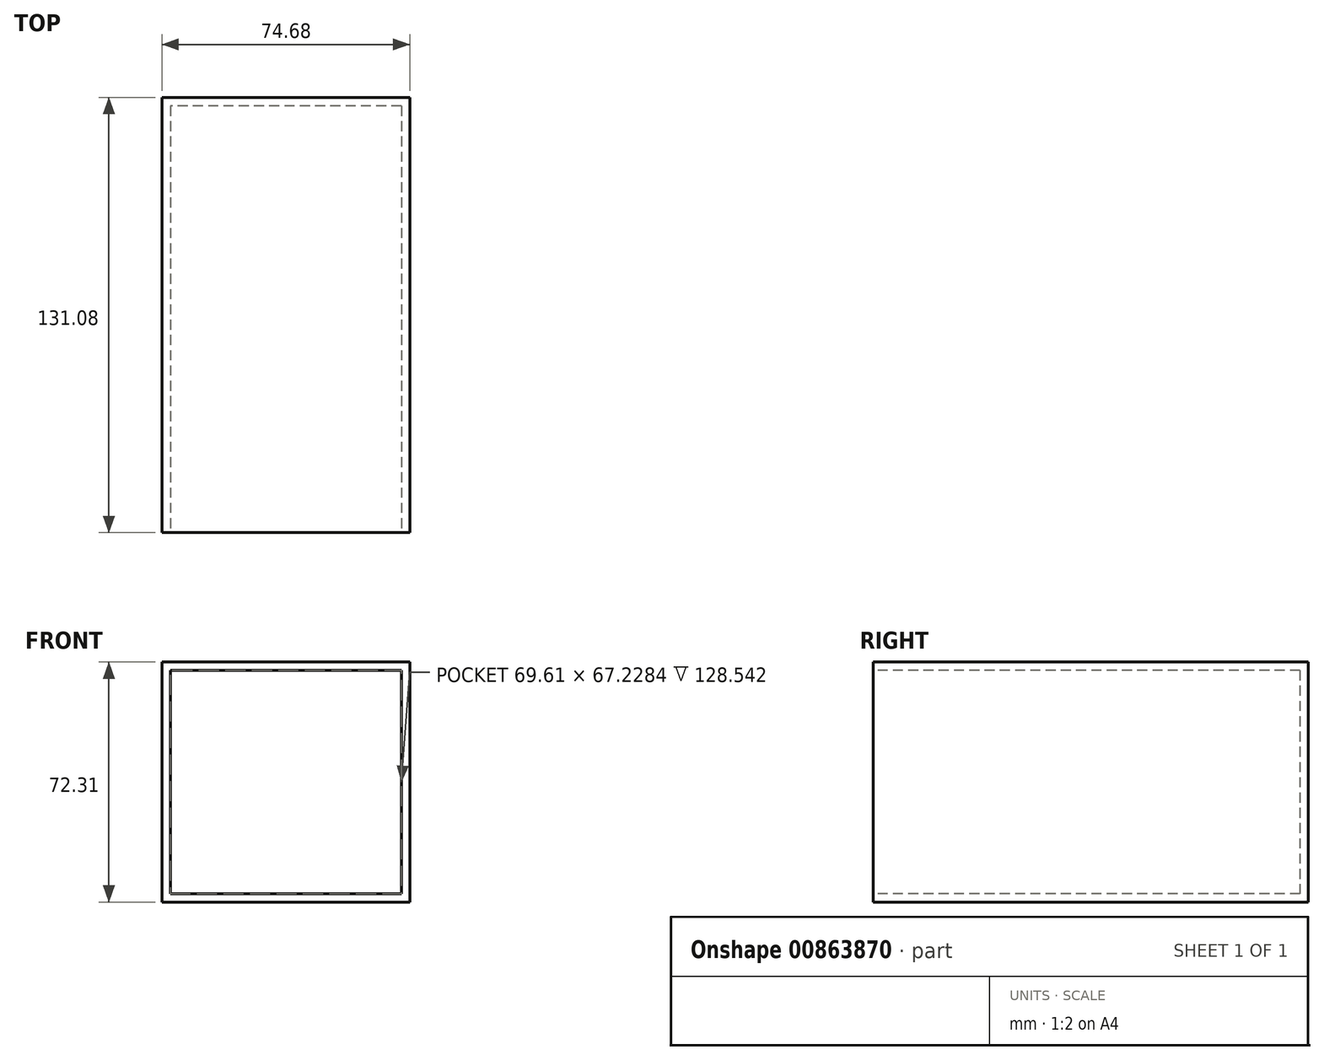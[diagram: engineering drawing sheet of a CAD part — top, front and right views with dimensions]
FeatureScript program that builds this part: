
annotation { "Feature Type Name" : "Feature", "Feature Type Description" : "" }
export const myFeature = defineFeature(function(context is Context, id is Id, definition is map)
    precondition{}
    {
        {
            var Q0;
            Q0=qCreatedBy(makeId("Top.planeOp"),FACE);
            var sketch = newSketch(context, id + "F0", { "sketchPlane" : qUnion([Q0])});
            skLineSegment(sketch, "E0.bottom", {"start": v(37.34, 65.54) * mm, "end": v(-37.34, 65.54) * mm});
            skLineSegment(sketch, "E0.top", {"start": v(37.34, -65.54) * mm, "end": v(-37.34, -65.54) * mm});
            skLineSegment(sketch, "E0.left", {"start": v(37.34, 65.54) * mm, "end": v(37.34, -65.54) * mm});
            skLineSegment(sketch, "E0.right", {"start": v(-37.34, 65.54) * mm, "end": v(-37.34, -65.54) * mm});
            skPoint(sketch, "E0.middle", {"position": v(0, 0) * mm});
            skSolve(sketch);
        }
        {
            var Q0;
            Q0=makeQuery(id+"F0.imprint","IMPRINT",FACE,{"disambiguationData":[TD([[makeQuery(id+"F0.imprint","IMPRINT",EDGE,{"derivedFrom":sQuery(id+"F0.wireOp",EDGE,"E0.bottom")}),1.0]])]});
            extrude(context, id + "F1", {"entities" : qUnion([Q0]), "depth" : 37.31 * mm, "offsetDistance" : 25.4 * mm});
        }
        {
            var Q0;
            Q0=makeQuery(id+"F1.opExtrude","CAP_FACE",FACE,{"disambiguationData":[OSD([sQuery(id+"F0.wireOp",EDGE,"E0.bottom"),sQuery(id+"F0.wireOp",EDGE,"E0.top"),sQuery(id+"F0.wireOp",EDGE,"E0.left"),sQuery(id+"F0.wireOp",EDGE,"E0.right")])],"isStart":true});
            extrude(context, id + "F2", {"entities" : qUnion([Q0]), "operationType" : NewBodyOperationType.ADD, "depth" : 35 * mm, "offsetDistance" : 25.4 * mm});
        }
        {
            var Q0;
            {var subQ0=sQuery(id+"F0.wireOp",EDGE,"E0.top");Q0=makeQuery(id+"F2.boolean.opBoolean","MERGE",FACE,{"derivedFrom":[makeQuery(id+"F1.opExtrude","SWEPT_FACE",FACE,{"disambiguationData":[OSD([subQ0])]}),makeQuery(id+"F2.opExtrude","SWEPT_FACE",FACE,{"disambiguationData":[OSD([subQ0])]})]});}
            shell(context, id + "F3", {"entities" : qUnion([Q0]), "thickness" : 2.54 * mm});
        }
        {
            var Q0;
            {var subQ0=sQuery(id+"F0.wireOp",EDGE,"E0.bottom");Q0=makeQuery(id+"F2.boolean.opBoolean","MERGE",FACE,{"derivedFrom":[makeQuery(id+"F1.opExtrude","SWEPT_FACE",FACE,{"disambiguationData":[OSD([subQ0])]}),makeQuery(id+"F2.opExtrude","SWEPT_FACE",FACE,{"disambiguationData":[OSD([subQ0])]})]});}
            cPlane(context, id + "F4", {"entities" : qUnion([Q0]), "cplaneType" : CPlaneType.OFFSET, "offset" : 0.33 * mm, "width" : 152.4 * mm, "height" : 152.4 * mm});
        }
    });
